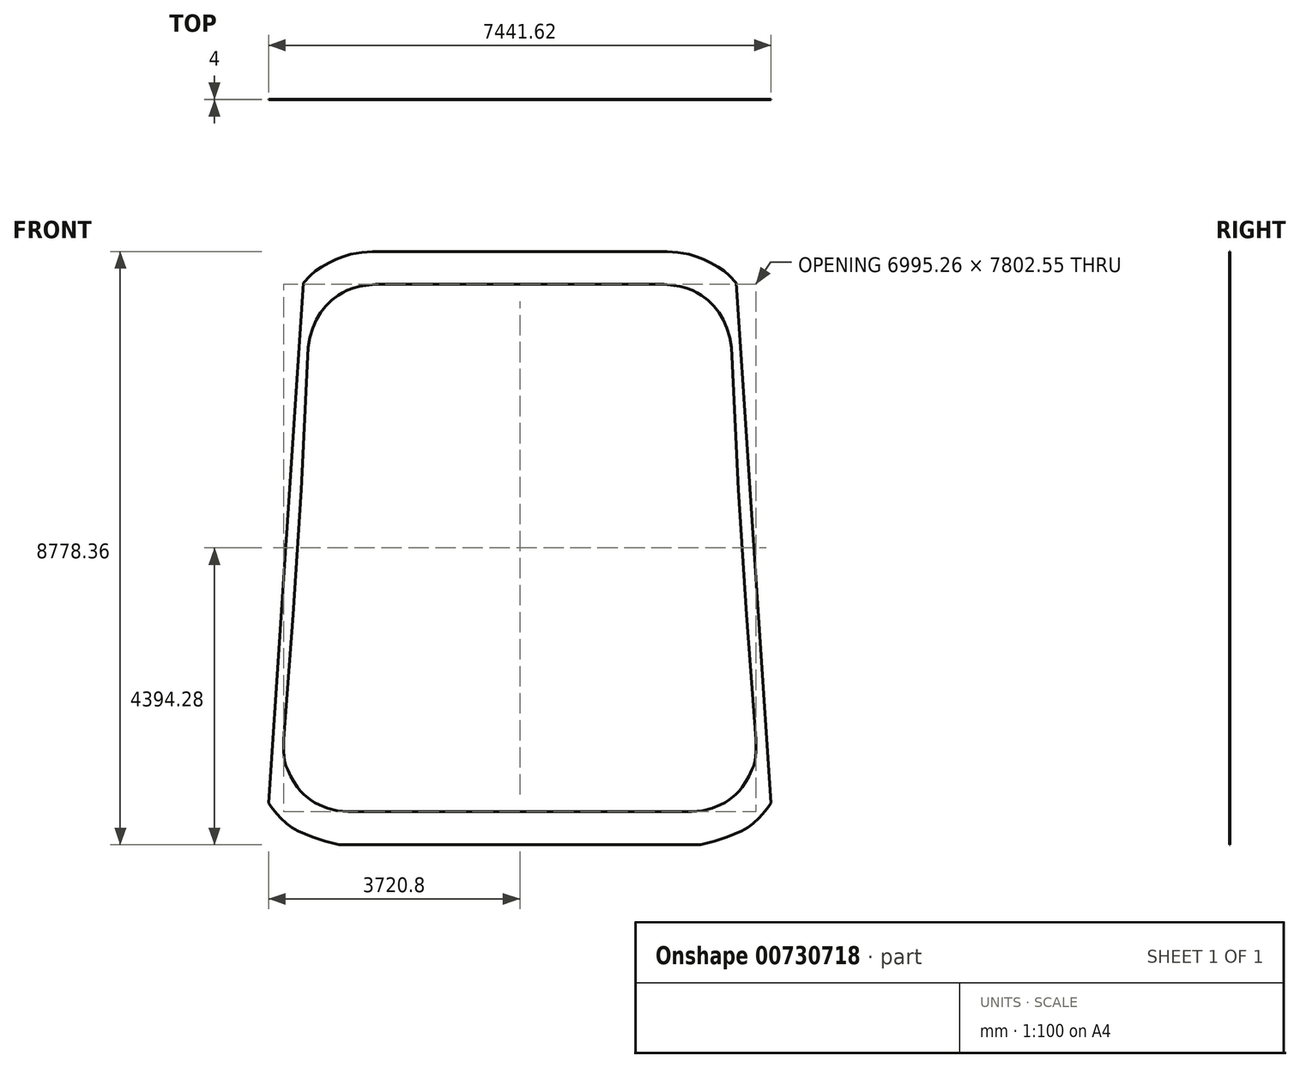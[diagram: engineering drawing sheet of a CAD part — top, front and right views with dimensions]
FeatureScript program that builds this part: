
annotation { "Feature Type Name" : "Feature", "Feature Type Description" : "" }
export const myFeature = defineFeature(function(context is Context, id is Id, definition is map)
    precondition{}
    {
        {
            var Q0;
            Q0=qCreatedBy(makeId("Front.planeOp"),FACE);
            var sketch = newSketch(context, id + "F0", { "sketchPlane" : qUnion([Q0])});
            skLineSegment(sketch, "E0", {"start": v(-3203.71, 3925.63) * mm, "end": v(-3077, 3917.12) * mm});
            skLineSegment(sketch, "E1", {"start": v(-3077, 3917.12) * mm, "end": v(-3203.71, 3925.63) * mm});
            skLineSegment(sketch, "E2", {"start": v(-3203.71, 3925.63) * mm, "end": v(-3103, 4031.73) * mm});
            skLineSegment(sketch, "E3", {"start": v(-3103, 4031.73) * mm, "end": v(-3022.71, 4100.16) * mm});
            skLineSegment(sketch, "E4", {"start": v(-3022.71, 4100.16) * mm, "end": v(-2936.5, 4160.74) * mm});
            skLineSegment(sketch, "E5", {"start": v(-2936.5, 4160.74) * mm, "end": v(-2819.74, 4226.37) * mm});
            skLineSegment(sketch, "E6", {"start": v(-2819.74, 4226.37) * mm, "end": v(-2721.55, 4273.84) * mm});
            skLineSegment(sketch, "E7", {"start": v(-2721.55, 4273.84) * mm, "end": v(-2620.5, 4314.38) * mm});
            skLineSegment(sketch, "E8", {"start": v(-2620.5, 4314.38) * mm, "end": v(-2502.2, 4349.08) * mm});
            skLineSegment(sketch, "E9", {"start": v(-2502.2, 4349.08) * mm, "end": v(-2421.04, 4366.1) * mm});
            skLineSegment(sketch, "E10", {"start": v(-2421.04, 4366.1) * mm, "end": v(-2339.02, 4377.78) * mm});
            skLineSegment(sketch, "E11", {"start": v(-2339.02, 4377.78) * mm, "end": v(-2180.63, 4386.6) * mm});
            skLineSegment(sketch, "E12", {"start": v(-2180.63, 4386.6) * mm, "end": v(-2061.93, 4386.62) * mm});
            skLineSegment(sketch, "E13", {"start": v(-2061.93, 4386.62) * mm, "end": v(-2061.9, 4259.62) * mm});
            skLineSegment(sketch, "E14", {"start": v(-2061.9, 4259.62) * mm, "end": v(-2061.93, 4386.62) * mm});
            skLineSegment(sketch, "E15", {"start": v(-2061.93, 4386.62) * mm, "end": v(-0.01, 4389.18) * mm});
            skLineSegment(sketch, "E16", {"start": v(-0.01, 4389.18) * mm, "end": v(0.14, 4262.18) * mm});
            skLineSegment(sketch, "E17", {"start": v(0.14, 4262.18) * mm, "end": v(-0.01, 4389.18) * mm});
            skLineSegment(sketch, "E18", {"start": v(-0.01, 4389.18) * mm, "end": v(2061.93, 4386.62) * mm});
            skLineSegment(sketch, "E19", {"start": v(2061.93, 4386.62) * mm, "end": v(2061.76, 4259.62) * mm});
            skLineSegment(sketch, "E20", {"start": v(2061.76, 4259.62) * mm, "end": v(2061.93, 4386.62) * mm});
            skLineSegment(sketch, "E21", {"start": v(2061.93, 4386.62) * mm, "end": v(2180.63, 4386.6) * mm});
            skLineSegment(sketch, "E22", {"start": v(2180.63, 4386.6) * mm, "end": v(2339, 4377.78) * mm});
            skLineSegment(sketch, "E23", {"start": v(2339, 4377.78) * mm, "end": v(2421.04, 4366.1) * mm});
            skLineSegment(sketch, "E24", {"start": v(2421.04, 4366.1) * mm, "end": v(2502.17, 4349.08) * mm});
            skLineSegment(sketch, "E25", {"start": v(2502.17, 4349.08) * mm, "end": v(2620.48, 4314.38) * mm});
            skLineSegment(sketch, "E26", {"start": v(2620.48, 4314.38) * mm, "end": v(2721.55, 4273.84) * mm});
            skLineSegment(sketch, "E27", {"start": v(2721.55, 4273.84) * mm, "end": v(2819.72, 4226.37) * mm});
            skLineSegment(sketch, "E28", {"start": v(2819.72, 4226.37) * mm, "end": v(2936.48, 4160.74) * mm});
            skLineSegment(sketch, "E29", {"start": v(2936.48, 4160.74) * mm, "end": v(3022.71, 4100.16) * mm});
            skLineSegment(sketch, "E30", {"start": v(3022.71, 4100.16) * mm, "end": v(3102.98, 4031.73) * mm});
            skLineSegment(sketch, "E31", {"start": v(3102.98, 4031.73) * mm, "end": v(3203.69, 3925.63) * mm});
            skLineSegment(sketch, "E32", {"start": v(3203.69, 3925.63) * mm, "end": v(3111.59, 3838.18) * mm});
            skLineSegment(sketch, "E33", {"start": v(3111.59, 3838.18) * mm, "end": v(3203.69, 3925.63) * mm});
            skLineSegment(sketch, "E34", {"start": v(3203.69, 3925.63) * mm, "end": v(3720.8, -3771.38) * mm});
            skLineSegment(sketch, "E35", {"start": v(3720.8, -3771.38) * mm, "end": v(3594.09, -3779.89) * mm});
            skLineSegment(sketch, "E36", {"start": v(3594.09, -3779.89) * mm, "end": v(3720.8, -3771.38) * mm});
            skLineSegment(sketch, "E37", {"start": v(3720.8, -3771.38) * mm, "end": v(3680.4, -3829.27) * mm});
            skLineSegment(sketch, "E38", {"start": v(3680.4, -3829.27) * mm, "end": v(3630.54, -3889.82) * mm});
            skLineSegment(sketch, "E39", {"start": v(3630.54, -3889.82) * mm, "end": v(3543.54, -3984.59) * mm});
            skLineSegment(sketch, "E40", {"start": v(3543.54, -3984.59) * mm, "end": v(3453.96, -4074.66) * mm});
            skLineSegment(sketch, "E41", {"start": v(3453.96, -4074.66) * mm, "end": v(3372.24, -4133.76) * mm});
            skLineSegment(sketch, "E42", {"start": v(3372.24, -4133.76) * mm, "end": v(3283.2, -4182.48) * mm});
            skLineSegment(sketch, "E43", {"start": v(3283.2, -4182.48) * mm, "end": v(3179.13, -4229.8) * mm});
            skLineSegment(sketch, "E44", {"start": v(3179.13, -4229.8) * mm, "end": v(3072.96, -4271.5) * mm});
            skLineSegment(sketch, "E45", {"start": v(3072.96, -4271.5) * mm, "end": v(2876.72, -4337.14) * mm});
            skLineSegment(sketch, "E46", {"start": v(2876.72, -4337.14) * mm, "end": v(2676.46, -4389.18) * mm});
            skLineSegment(sketch, "E47", {"start": v(2676.46, -4389.18) * mm, "end": v(2644.5, -4266.27) * mm});
            skLineSegment(sketch, "E48", {"start": v(2644.5, -4266.27) * mm, "end": v(2676.46, -4389.18) * mm});
            skLineSegment(sketch, "E49", {"start": v(2676.46, -4389.18) * mm, "end": v(-0.01, -4389.18) * mm});
            skLineSegment(sketch, "E50", {"start": v(-0.01, -4389.18) * mm, "end": v(-0.01, -4262.18) * mm});
            skLineSegment(sketch, "E51", {"start": v(-0.01, -4262.18) * mm, "end": v(-0.01, -4389.18) * mm});
            skLineSegment(sketch, "E52", {"start": v(-0.01, -4389.18) * mm, "end": v(-2676.46, -4389.18) * mm});
            skLineSegment(sketch, "E53", {"start": v(-2676.46, -4389.18) * mm, "end": v(-2676.46, -4262.18) * mm});
            skLineSegment(sketch, "E54", {"start": v(-2676.46, -4262.18) * mm, "end": v(-2676.46, -4389.18) * mm});
            skLineSegment(sketch, "E55", {"start": v(-2676.46, -4389.18) * mm, "end": v(-2876.74, -4337.14) * mm});
            skLineSegment(sketch, "E56", {"start": v(-2876.74, -4337.14) * mm, "end": v(-3072.98, -4271.5) * mm});
            skLineSegment(sketch, "E57", {"start": v(-3072.98, -4271.5) * mm, "end": v(-3179.15, -4229.8) * mm});
            skLineSegment(sketch, "E58", {"start": v(-3179.15, -4229.8) * mm, "end": v(-3283.22, -4182.48) * mm});
            skLineSegment(sketch, "E59", {"start": v(-3283.22, -4182.48) * mm, "end": v(-3372.27, -4133.76) * mm});
            skLineSegment(sketch, "E60", {"start": v(-3372.27, -4133.76) * mm, "end": v(-3453.98, -4074.66) * mm});
            skLineSegment(sketch, "E61", {"start": v(-3453.98, -4074.66) * mm, "end": v(-3543.57, -3984.59) * mm});
            skLineSegment(sketch, "E62", {"start": v(-3543.57, -3984.59) * mm, "end": v(-3630.56, -3889.82) * mm});
            skLineSegment(sketch, "E63", {"start": v(-3630.56, -3889.82) * mm, "end": v(-3680.42, -3829.27) * mm});
            skLineSegment(sketch, "E64", {"start": v(-3680.42, -3829.27) * mm, "end": v(-3720.8, -3771.38) * mm});
            skLineSegment(sketch, "E65", {"start": v(-3720.8, -3771.38) * mm, "end": v(-3616.67, -3698.7) * mm});
            skLineSegment(sketch, "E66", {"start": v(-3616.67, -3698.7) * mm, "end": v(-3720.8, -3771.38) * mm});
            skLineSegment(sketch, "E67", {"start": v(-3720.8, -3771.38) * mm, "end": v(-3203.71, 3925.63) * mm});
            skLineSegment(sketch, "E68", {"start": v(-3132.67, 2974.84) * mm, "end": v(-3005.8, 2969.27) * mm});
            skLineSegment(sketch, "E69", {"start": v(-3005.8, 2969.27) * mm, "end": v(-3132.67, 2974.84) * mm});
            skLineSegment(sketch, "E70", {"start": v(-3132.67, 2974.84) * mm, "end": v(-3106.15, 3118.93) * mm});
            skLineSegment(sketch, "E71", {"start": v(-3106.15, 3118.93) * mm, "end": v(-3063.63, 3259.32) * mm});
            skLineSegment(sketch, "E72", {"start": v(-3063.63, 3259.32) * mm, "end": v(-3010.9, 3381.74) * mm});
            skLineSegment(sketch, "E73", {"start": v(-3010.9, 3381.74) * mm, "end": v(-2948.32, 3486.54) * mm});
            skLineSegment(sketch, "E74", {"start": v(-2948.32, 3486.54) * mm, "end": v(-2873.1, 3580.7) * mm});
            skLineSegment(sketch, "E75", {"start": v(-2873.1, 3580.7) * mm, "end": v(-2784.51, 3668.74) * mm});
            skLineSegment(sketch, "E76", {"start": v(-2784.51, 3668.74) * mm, "end": v(-2690.56, 3738.56) * mm});
            skLineSegment(sketch, "E77", {"start": v(-2690.56, 3738.56) * mm, "end": v(-2623.76, 3782.15) * mm});
            skLineSegment(sketch, "E78", {"start": v(-2623.76, 3782.15) * mm, "end": v(-2553.78, 3819.56) * mm});
            skLineSegment(sketch, "E79", {"start": v(-2553.78, 3819.56) * mm, "end": v(-2465.67, 3851.06) * mm});
            skLineSegment(sketch, "E80", {"start": v(-2465.67, 3851.06) * mm, "end": v(-2373.9, 3871.76) * mm});
            skLineSegment(sketch, "E81", {"start": v(-2373.9, 3871.76) * mm, "end": v(-2275.52, 3887.33) * mm});
            skLineSegment(sketch, "E82", {"start": v(-2275.52, 3887.33) * mm, "end": v(-2135.16, 3906.38) * mm});
            skLineSegment(sketch, "E83", {"start": v(-2135.16, 3906.38) * mm, "end": v(-2118.1, 3780.52) * mm});
            skLineSegment(sketch, "E84", {"start": v(-2118.1, 3780.52) * mm, "end": v(-2135.16, 3906.38) * mm});
            skLineSegment(sketch, "E85", {"start": v(-2135.16, 3906.38) * mm, "end": v(-0.01, 3906.38) * mm});
            skLineSegment(sketch, "E86", {"start": v(-0.01, 3906.38) * mm, "end": v(-0.01, 3779.38) * mm});
            skLineSegment(sketch, "E87", {"start": v(-0.01, 3779.38) * mm, "end": v(-0.01, 3906.38) * mm});
            skLineSegment(sketch, "E88", {"start": v(-0.01, 3906.38) * mm, "end": v(2135.14, 3906.38) * mm});
            skLineSegment(sketch, "E89", {"start": v(2135.14, 3906.38) * mm, "end": v(2135.14, 3779.38) * mm});
            skLineSegment(sketch, "E90", {"start": v(2135.14, 3779.38) * mm, "end": v(2135.14, 3906.38) * mm});
            skLineSegment(sketch, "E91", {"start": v(2135.14, 3906.38) * mm, "end": v(2275.5, 3887.33) * mm});
            skLineSegment(sketch, "E92", {"start": v(2275.5, 3887.33) * mm, "end": v(2373.9, 3871.76) * mm});
            skLineSegment(sketch, "E93", {"start": v(2373.9, 3871.76) * mm, "end": v(2465.64, 3851.06) * mm});
            skLineSegment(sketch, "E94", {"start": v(2465.64, 3851.06) * mm, "end": v(2553.78, 3819.56) * mm});
            skLineSegment(sketch, "E95", {"start": v(2553.78, 3819.56) * mm, "end": v(2623.76, 3782.15) * mm});
            skLineSegment(sketch, "E96", {"start": v(2623.76, 3782.15) * mm, "end": v(2690.53, 3738.56) * mm});
            skLineSegment(sketch, "E97", {"start": v(2690.53, 3738.56) * mm, "end": v(2784.49, 3668.74) * mm});
            skLineSegment(sketch, "E98", {"start": v(2784.49, 3668.74) * mm, "end": v(2873.08, 3580.7) * mm});
            skLineSegment(sketch, "E99", {"start": v(2873.08, 3580.7) * mm, "end": v(2948.3, 3486.54) * mm});
            skLineSegment(sketch, "E100", {"start": v(2948.3, 3486.54) * mm, "end": v(3010.88, 3381.74) * mm});
            skLineSegment(sketch, "E101", {"start": v(3010.88, 3381.74) * mm, "end": v(3063.6, 3259.32) * mm});
            skLineSegment(sketch, "E102", {"start": v(3063.6, 3259.32) * mm, "end": v(3106.13, 3118.93) * mm});
            skLineSegment(sketch, "E103", {"start": v(3106.13, 3118.93) * mm, "end": v(3132.67, 2974.84) * mm});
            skLineSegment(sketch, "E104", {"start": v(3132.67, 2974.84) * mm, "end": v(3007.75, 2951.82) * mm});
            skLineSegment(sketch, "E105", {"start": v(3007.75, 2951.82) * mm, "end": v(3132.67, 2974.84) * mm});
            skLineSegment(sketch, "E106", {"start": v(3132.67, 2974.84) * mm, "end": v(3144.08, 2713.72) * mm});
            skLineSegment(sketch, "E107", {"start": v(3144.08, 2713.72) * mm, "end": v(3238.46, 864.43) * mm});
            skLineSegment(sketch, "E108", {"start": v(3238.46, 864.43) * mm, "end": v(3356.32, -983.58) * mm});
            skLineSegment(sketch, "E109", {"start": v(3356.32, -983.58) * mm, "end": v(3497.62, -2829.88) * mm});
            skLineSegment(sketch, "E110", {"start": v(3497.62, -2829.88) * mm, "end": v(3370.97, -2839.58) * mm});
            skLineSegment(sketch, "E111", {"start": v(3370.97, -2839.58) * mm, "end": v(3497.62, -2829.88) * mm});
            skLineSegment(sketch, "E112", {"start": v(3497.62, -2829.88) * mm, "end": v(3496.04, -3009.63) * mm});
            skLineSegment(sketch, "E113", {"start": v(3496.04, -3009.63) * mm, "end": v(3491.45, -3077.65) * mm});
            skLineSegment(sketch, "E114", {"start": v(3491.45, -3077.65) * mm, "end": v(3481.62, -3144.81) * mm});
            skLineSegment(sketch, "E115", {"start": v(3481.62, -3144.81) * mm, "end": v(3462.03, -3215.32) * mm});
            skLineSegment(sketch, "E116", {"start": v(3462.03, -3215.32) * mm, "end": v(3435.26, -3283.72) * mm});
            skLineSegment(sketch, "E117", {"start": v(3435.26, -3283.72) * mm, "end": v(3394.95, -3368.26) * mm});
            skLineSegment(sketch, "E118", {"start": v(3394.95, -3368.26) * mm, "end": v(3349.69, -3450.12) * mm});
            skLineSegment(sketch, "E119", {"start": v(3349.69, -3450.12) * mm, "end": v(3293.53, -3537.4) * mm});
            skLineSegment(sketch, "E120", {"start": v(3293.53, -3537.4) * mm, "end": v(3248.06, -3593.68) * mm});
            skLineSegment(sketch, "E121", {"start": v(3248.06, -3593.68) * mm, "end": v(3197.31, -3645.37) * mm});
            skLineSegment(sketch, "E122", {"start": v(3197.31, -3645.37) * mm, "end": v(3102.06, -3721.5) * mm});
            skLineSegment(sketch, "E123", {"start": v(3102.06, -3721.5) * mm, "end": v(3037.67, -3762.26) * mm});
            skLineSegment(sketch, "E124", {"start": v(3037.67, -3762.26) * mm, "end": v(2970.26, -3797.82) * mm});
            skLineSegment(sketch, "E125", {"start": v(2970.26, -3797.82) * mm, "end": v(2850.8, -3845.8) * mm});
            skLineSegment(sketch, "E126", {"start": v(2850.8, -3845.8) * mm, "end": v(2700.19, -3882.45) * mm});
            skLineSegment(sketch, "E127", {"start": v(2700.19, -3882.45) * mm, "end": v(2545.9, -3896.17) * mm});
            skLineSegment(sketch, "E128", {"start": v(2545.9, -3896.17) * mm, "end": v(2534.65, -3769.68) * mm});
            skLineSegment(sketch, "E129", {"start": v(2534.65, -3769.68) * mm, "end": v(2545.9, -3896.17) * mm});
            skLineSegment(sketch, "E130", {"start": v(2545.9, -3896.17) * mm, "end": v(-0.01, -3896.17) * mm});
            skLineSegment(sketch, "E131", {"start": v(-0.01, -3896.17) * mm, "end": v(-0.01, -3769.17) * mm});
            skLineSegment(sketch, "E132", {"start": v(-0.01, -3769.17) * mm, "end": v(-0.01, -3896.17) * mm});
            skLineSegment(sketch, "E133", {"start": v(-0.01, -3896.17) * mm, "end": v(-2545.9, -3896.17) * mm});
            skLineSegment(sketch, "E134", {"start": v(-2545.9, -3896.17) * mm, "end": v(-2545.9, -3769.17) * mm});
            skLineSegment(sketch, "E135", {"start": v(-2545.9, -3769.17) * mm, "end": v(-2545.9, -3896.17) * mm});
            skLineSegment(sketch, "E136", {"start": v(-2545.9, -3896.17) * mm, "end": v(-2700.21, -3882.45) * mm});
            skLineSegment(sketch, "E137", {"start": v(-2700.21, -3882.45) * mm, "end": v(-2850.83, -3845.8) * mm});
            skLineSegment(sketch, "E138", {"start": v(-2850.83, -3845.8) * mm, "end": v(-2970.29, -3797.82) * mm});
            skLineSegment(sketch, "E139", {"start": v(-2970.29, -3797.82) * mm, "end": v(-3037.7, -3762.26) * mm});
            skLineSegment(sketch, "E140", {"start": v(-3037.7, -3762.26) * mm, "end": v(-3102.09, -3721.5) * mm});
            skLineSegment(sketch, "E141", {"start": v(-3102.09, -3721.5) * mm, "end": v(-3197.34, -3645.37) * mm});
            skLineSegment(sketch, "E142", {"start": v(-3197.34, -3645.37) * mm, "end": v(-3248.06, -3593.68) * mm});
            skLineSegment(sketch, "E143", {"start": v(-3248.06, -3593.68) * mm, "end": v(-3293.55, -3537.4) * mm});
            skLineSegment(sketch, "E144", {"start": v(-3293.55, -3537.4) * mm, "end": v(-3349.71, -3450.12) * mm});
            skLineSegment(sketch, "E145", {"start": v(-3349.71, -3450.12) * mm, "end": v(-3394.98, -3368.26) * mm});
            skLineSegment(sketch, "E146", {"start": v(-3394.98, -3368.26) * mm, "end": v(-3435.26, -3283.72) * mm});
            skLineSegment(sketch, "E147", {"start": v(-3435.26, -3283.72) * mm, "end": v(-3462.06, -3215.32) * mm});
            skLineSegment(sketch, "E148", {"start": v(-3462.06, -3215.32) * mm, "end": v(-3481.62, -3144.81) * mm});
            skLineSegment(sketch, "E149", {"start": v(-3481.62, -3144.81) * mm, "end": v(-3491.45, -3077.65) * mm});
            skLineSegment(sketch, "E150", {"start": v(-3491.45, -3077.65) * mm, "end": v(-3496.07, -3009.63) * mm});
            skLineSegment(sketch, "E151", {"start": v(-3496.07, -3009.63) * mm, "end": v(-3497.64, -2829.88) * mm});
            skLineSegment(sketch, "E152", {"start": v(-3497.64, -2829.88) * mm, "end": v(-3370.64, -2828.79) * mm});
            skLineSegment(sketch, "E153", {"start": v(-3370.64, -2828.79) * mm, "end": v(-3497.64, -2829.88) * mm});
            skLineSegment(sketch, "E154", {"start": v(-3497.64, -2829.88) * mm, "end": v(-3356.34, -983.58) * mm});
            skLineSegment(sketch, "E155", {"start": v(-3356.34, -983.58) * mm, "end": v(-3238.49, 864.43) * mm});
            skLineSegment(sketch, "E156", {"start": v(-3238.49, 864.43) * mm, "end": v(-3144.1, 2713.72) * mm});
            skLineSegment(sketch, "E157", {"start": v(-3144.1, 2713.72) * mm, "end": v(-3132.67, 2974.84) * mm});
            skSolve(sketch);
        }
        {
            var Q0;
            Q0=makeQuery(id+"F0.imprint","IMPRINT",FACE,{"disambiguationData":[TD([[makeQuery(id+"F0.imprint","IMPRINT",EDGE,{"derivedFrom":sQuery(id+"F0.wireOp",EDGE,"E2")}),-1.0]])]});
            extrude(context, id + "F1", {"entities" : qUnion([Q0]), "depth" : 4 * mm, "offsetDistance" : 25 * mm});
        }
    });
